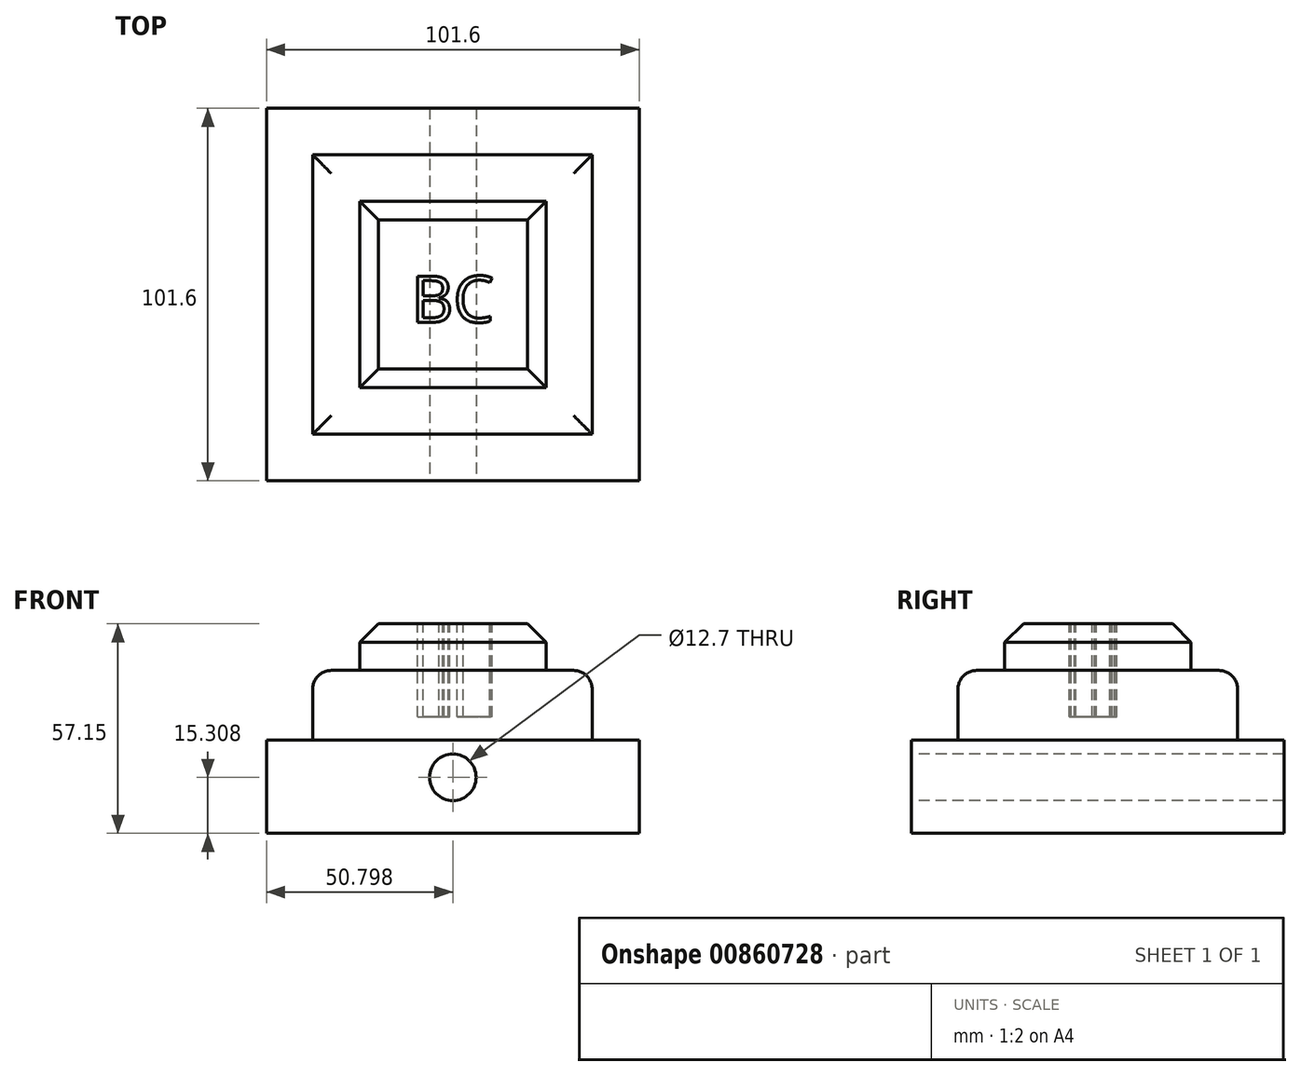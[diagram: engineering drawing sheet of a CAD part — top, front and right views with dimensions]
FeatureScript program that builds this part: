
annotation { "Feature Type Name" : "Feature", "Feature Type Description" : "" }
export const myFeature = defineFeature(function(context is Context, id is Id, definition is map)
    precondition{}
    {
        {
            var Q0;
            Q0=qCreatedBy(makeId("Top.planeOp"),FACE);
            var sketch = newSketch(context, id + "F0", { "sketchPlane" : qUnion([Q0])});
            skLineSegment(sketch, "E0.bottom", {"start": v(0, 0) * mm, "end": v(101.6, 0) * mm});
            skLineSegment(sketch, "E0.top", {"start": v(0, 101.6) * mm, "end": v(101.6, 101.6) * mm});
            skLineSegment(sketch, "E0.left", {"start": v(0, 0) * mm, "end": v(0, 101.6) * mm});
            skLineSegment(sketch, "E0.right", {"start": v(101.6, 0) * mm, "end": v(101.6, 101.6) * mm});
            skSolve(sketch);
        }
        {
            var Q0;
            Q0 = qSketchRegion(id + "F0", true);
            extrude(context, id + "F1", {"entities" : qUnion([Q0]), "depth" : 25.4 * mm, "offsetDistance" : 25.4 * mm});
        }
        {
            var Q0;
            Q0=makeQuery(id+"F1.opExtrude","CAP_FACE",FACE,{"disambiguationData":[OSD([sQuery(id+"F0.wireOp",EDGE,"E0.bottom"),sQuery(id+"F0.wireOp",EDGE,"E0.top"),sQuery(id+"F0.wireOp",EDGE,"E0.left"),sQuery(id+"F0.wireOp",EDGE,"E0.right")])],"isStart":false});
            var sketch = newSketch(context, id + "F2", { "sketchPlane" : qUnion([Q0])});
            skLineSegment(sketch, "E1.bottom", {"start": v(12.59, 12.72) * mm, "end": v(88.79, 12.72) * mm});
            skLineSegment(sketch, "E1.top", {"start": v(12.59, 88.92) * mm, "end": v(88.79, 88.92) * mm});
            skLineSegment(sketch, "E1.left", {"start": v(12.59, 12.72) * mm, "end": v(12.59, 88.92) * mm});
            skLineSegment(sketch, "E1.right", {"start": v(88.79, 12.72) * mm, "end": v(88.79, 88.92) * mm});
            skLineSegment(sketch, "E2", {"start": v(12.59, 56.04) * mm, "end": v(12.7, 56.04) * mm});
            skLineSegment(sketch, "E3", {"start": v(56.04, 88.92) * mm, "end": v(56.04, 88.9) * mm});
            skSolve(sketch);
        }
        {
            var Q0;
            Q0=makeQuery(id+"F2.imprint","IMPRINT",FACE,{"disambiguationData":[TD([[makeQuery(id+"F2.imprint","IMPRINT",EDGE,{"derivedFrom":sQuery(id+"F2.wireOp",EDGE,"E1.bottom")}),1.0]])]});
            extrude(context, id + "F3", {"entities" : qUnion([Q0]), "operationType" : NewBodyOperationType.ADD, "depth" : 19.05 * mm, "offsetDistance" : 25.4 * mm});
        }
        {
            var Q0;
            Q0=makeQuery(id+"F3.opExtrude","CAP_FACE",FACE,{"disambiguationData":[OSD([sQuery(id+"F2.wireOp",EDGE,"E1.bottom"),sQuery(id+"F2.wireOp",EDGE,"E1.top"),sQuery(id+"F2.wireOp",EDGE,"E1.left"),sQuery(id+"F2.wireOp",EDGE,"E1.right")])],"isStart":false});
            var sketch = newSketch(context, id + "F4", { "sketchPlane" : qUnion([Q0])});
            skLineSegment(sketch, "E4", {"start": v(50.69, 76.27) * mm, "end": v(50.69, 76.22) * mm});
            skLineSegment(sketch, "E5.bottom", {"start": v(25.46, 76.27) * mm, "end": v(76.26, 76.27) * mm});
            skLineSegment(sketch, "E5.top", {"start": v(25.46, 25.47) * mm, "end": v(76.26, 25.47) * mm});
            skLineSegment(sketch, "E5.left", {"start": v(25.46, 76.27) * mm, "end": v(25.46, 25.47) * mm});
            skLineSegment(sketch, "E5.right", {"start": v(76.26, 76.27) * mm, "end": v(76.26, 25.47) * mm});
            skPoint(sketch, "E6.start.orphan", {"position": v(12.59, 50.82) * mm});
            skPoint(sketch, "E7.orphan", {"position": v(50.69, 88.92) * mm});
            skSolve(sketch);
        }
        {
            var Q0;
            Q0=makeQuery(id+"F4.imprint","IMPRINT",FACE,{"disambiguationData":[TD([[makeQuery(id+"F4.imprint","IMPRINT",EDGE,{"derivedFrom":sQuery(id+"F4.wireOp",EDGE,"E5.top")}),1.0]])]});
            extrude(context, id + "F5", {"entities" : qUnion([Q0]), "operationType" : NewBodyOperationType.ADD, "depth" : 12.7 * mm, "offsetDistance" : 25.4 * mm});
        }
        {
            var Q0;
            Q0=makeQuery(id+"F1.opExtrude","SWEPT_FACE",FACE,{"disambiguationData":[OSD([sQuery(id+"F0.wireOp",EDGE,"E0.bottom")])]});
            var sketch = newSketch(context, id + "F6", { "sketchPlane" : qUnion([Q0])});
            skCircle(sketch, "E8", {"center": v(50.8, 15.3) * mm, "radius": 6.35 * mm});
            skPoint(sketch, "E9.start.orphan", {"position": v(0, 12.7) * mm});
            skPoint(sketch, "E10.start.orphan", {"position": v(101.6, 12.7) * mm});
            skSolve(sketch);
        }
        {
            var Q0;
            Q0=makeQuery(id+"F6.imprint","IMPRINT",FACE,{"disambiguationData":[TD([[makeQuery(id+"F6.imprint","IMPRINT",EDGE,{"derivedFrom":sQuery(id+"F6.wireOp",EDGE,"E8")}),1.0]])]});
            extrude(context, id + "F7", {"entities" : qUnion([Q0]), "operationType" : NewBodyOperationType.REMOVE, "oppositeDirection" : true, "depth" : 121.16 * mm, "offsetDistance" : 25.4 * mm});
        }
        {
            var Q0;
            Q0=makeQuery(id+"F5.opExtrude","CAP_FACE",FACE,{"disambiguationData":[OSD([sQuery(id+"F4.wireOp",EDGE,"E5.bottom"),sQuery(id+"F4.wireOp",EDGE,"E5.top"),sQuery(id+"F4.wireOp",EDGE,"E5.left"),sQuery(id+"F4.wireOp",EDGE,"E5.right")])],"isStart":false});
            var sketch = newSketch(context, id + "F8", { "sketchPlane" : qUnion([Q0])});
            skText(sketch, "E11", { "text": "BC", "fontName": "OpenSans-Regular.ttf"});
            const initialGuessF8  = {"E11": [0.0395, 0.04327, 1, 0, 0.0127]};
            skSetInitialGuess(sketch, initialGuessF8);
            skSolve(sketch);
        }
        {
            var Q0;
            Q0 = qSketchRegion(id + "F8", true);
            extrude(context, id + "F9", {"entities" : qUnion([Q0]), "operationType" : NewBodyOperationType.REMOVE, "oppositeDirection" : true, "depth" : 25.4 * mm, "offsetDistance" : 25.4 * mm});
        }
        {
            var Q0;
            Q0=makeQuery(id+"F3.opExtrude","CAP_EDGE",EDGE,{"disambiguationData":[OSD([sQuery(id+"F2.wireOp",EDGE,"E1.bottom")])],"isStart":false});
            var Q1;
            Q1=makeQuery(id+"F3.opExtrude","CAP_EDGE",EDGE,{"disambiguationData":[OSD([sQuery(id+"F2.wireOp",EDGE,"E1.left")])],"isStart":false});
            var Q2;
            Q2=makeQuery(id+"F3.opExtrude","CAP_EDGE",EDGE,{"disambiguationData":[OSD([sQuery(id+"F2.wireOp",EDGE,"E1.top")])],"isStart":false});
            var Q3;
            Q3=makeQuery(id+"F3.opExtrude","CAP_EDGE",EDGE,{"disambiguationData":[OSD([sQuery(id+"F2.wireOp",EDGE,"E1.right")])],"isStart":false});
            fillet(context, id + "F10", {"entities" : qUnion([Q0, Q1, Q2, Q3]), "radius" : 5.08 * mm, "tangentPropagation" : true, "allowEdgeOverflow" : false});
        }
        {
            var Q0;
            Q0=makeQuery(id+"F5.opExtrude","CAP_EDGE",EDGE,{"disambiguationData":[OSD([sQuery(id+"F4.wireOp",EDGE,"E5.top")])],"isStart":false});
            var Q1;
            Q1=makeQuery(id+"F5.opExtrude","CAP_EDGE",EDGE,{"disambiguationData":[OSD([sQuery(id+"F4.wireOp",EDGE,"E5.right")])],"isStart":false});
            var Q2;
            Q2=makeQuery(id+"F5.opExtrude","CAP_EDGE",EDGE,{"disambiguationData":[OSD([sQuery(id+"F4.wireOp",EDGE,"E5.bottom")])],"isStart":false});
            var Q3;
            Q3=makeQuery(id+"F5.opExtrude","CAP_EDGE",EDGE,{"disambiguationData":[OSD([sQuery(id+"F4.wireOp",EDGE,"E5.left")])],"isStart":false});
            chamfer(context, id + "F11", {"entities" : qUnion([Q0, Q1, Q2, Q3]), "width" : 5.08 * mm, "tangentPropagation" : true});
        }
    });
